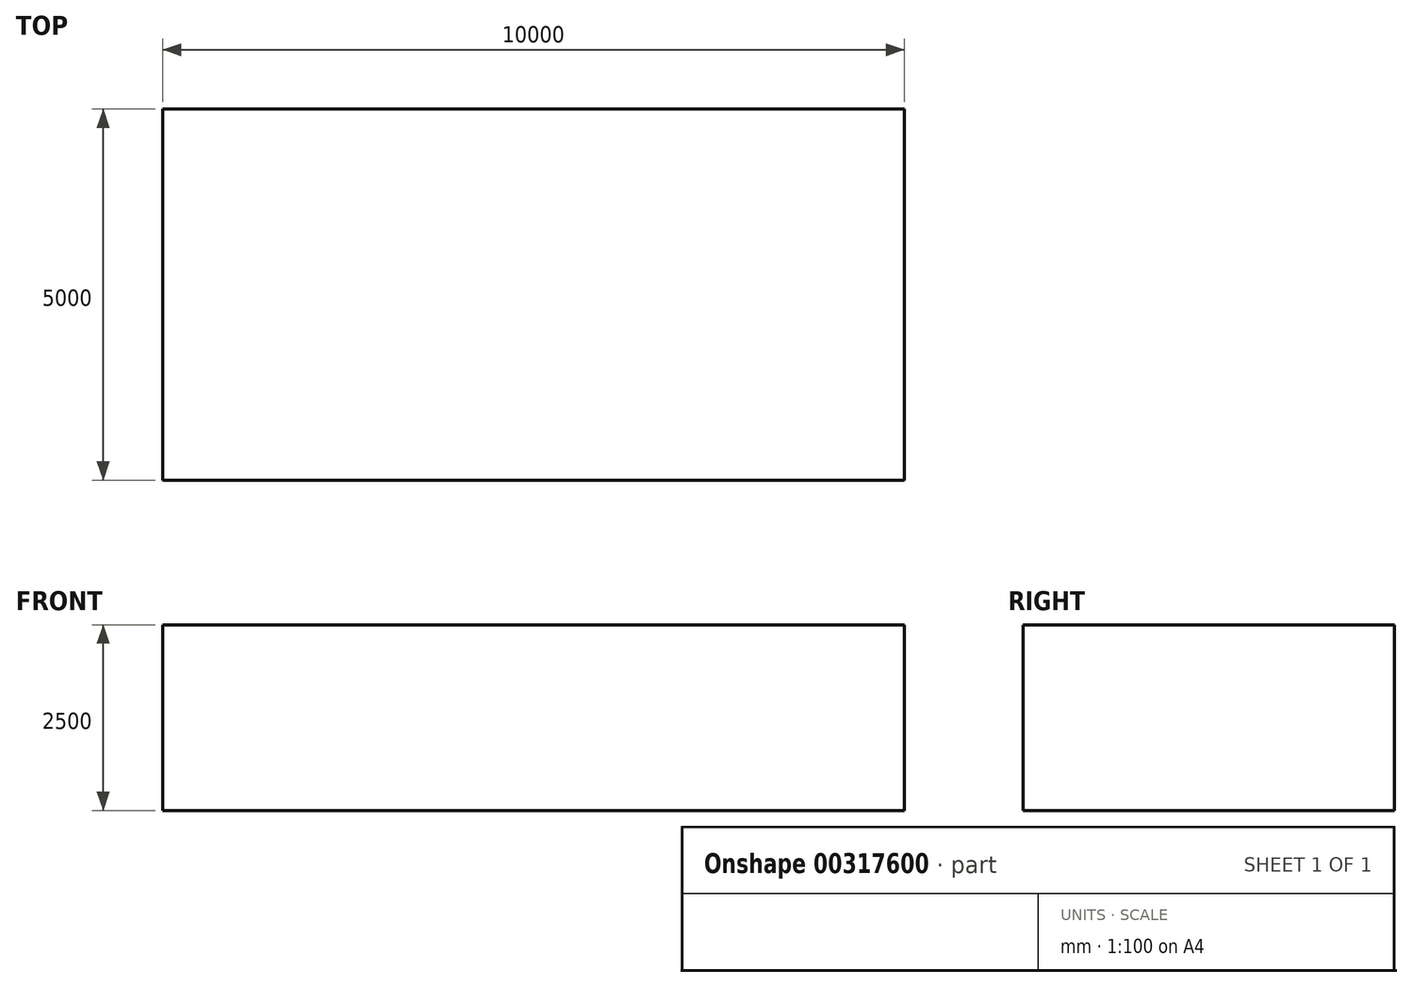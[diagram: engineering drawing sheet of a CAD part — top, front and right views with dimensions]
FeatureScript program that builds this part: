
annotation { "Feature Type Name" : "Feature", "Feature Type Description" : "" }
export const myFeature = defineFeature(function(context is Context, id is Id, definition is map)
    precondition{}
    {
        {
            var Q0;
            Q0=qCreatedBy(makeId("Front.planeOp"),FACE);
            var sketch = newSketch(context, id + "F0", { "sketchPlane" : qUnion([Q0])});
            skLineSegment(sketch, "E0", {"start": v(0, 0) * mm, "end": v(0, -2500) * mm});
            skLineSegment(sketch, "E1", {"start": v(0, 0) * mm, "end": v(10000, 0) * mm});
            skLineSegment(sketch, "E2", {"start": v(10000, 0) * mm, "end": v(10000, -2500) * mm});
            skLineSegment(sketch, "E3", {"start": v(10000, -2500) * mm, "end": v(0, -2500) * mm});
            skSolve(sketch);
        }
        {
            var Q0;
            Q0 = qSketchRegion(id + "F0", true);
            extrude(context, id + "F1", {"entities" : qUnion([Q0]), "depth" : 5000 * mm});
        }
    });
